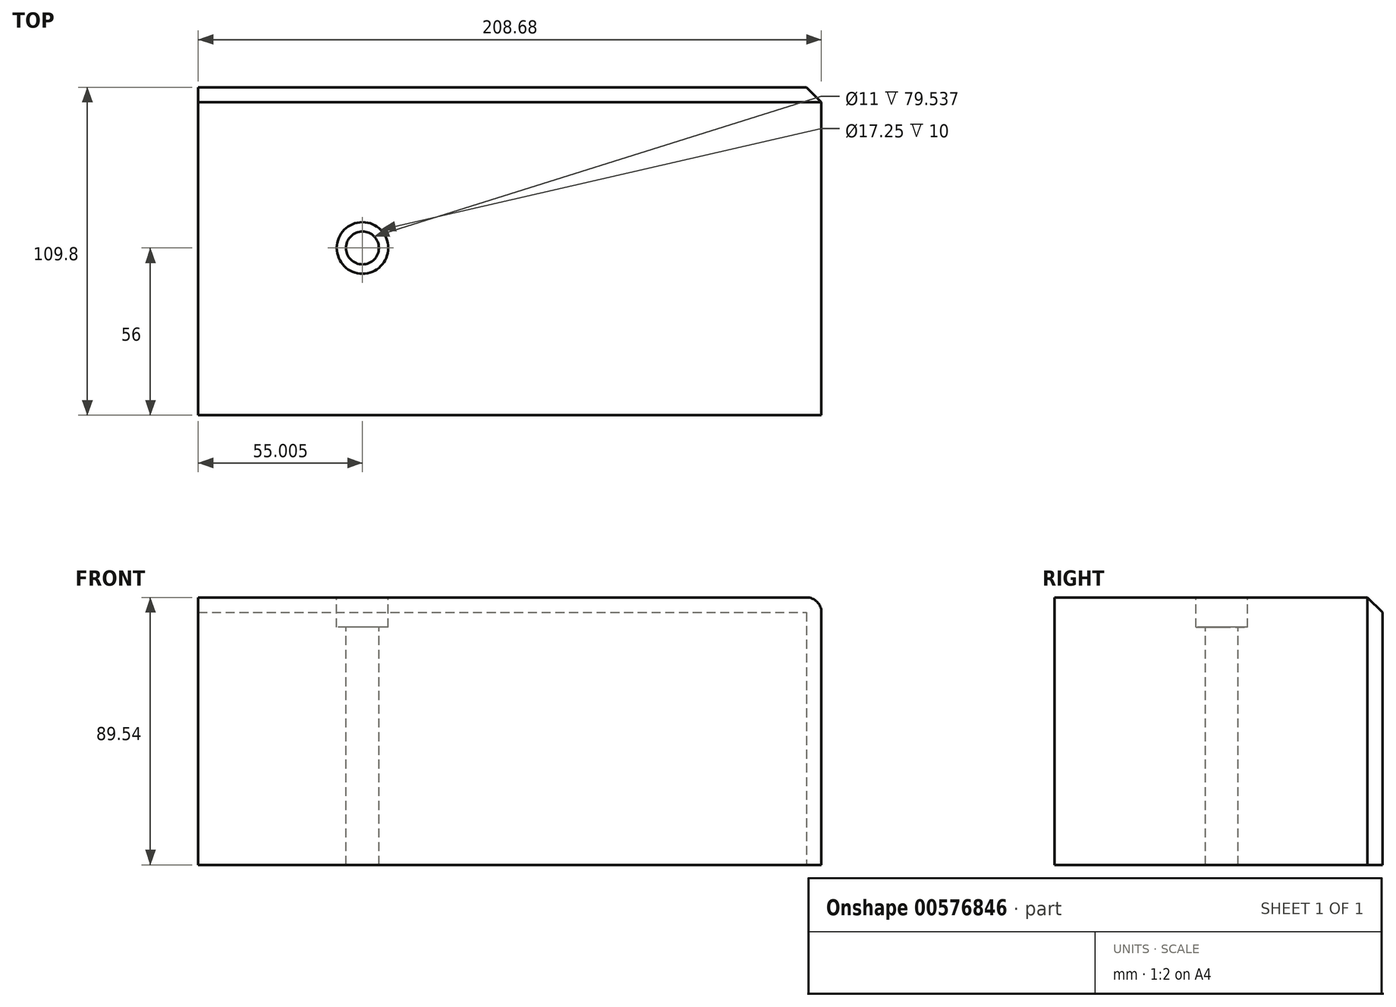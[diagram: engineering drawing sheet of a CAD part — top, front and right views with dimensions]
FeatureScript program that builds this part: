
annotation { "Feature Type Name" : "Feature", "Feature Type Description" : "" }
export const myFeature = defineFeature(function(context is Context, id is Id, definition is map)
    precondition{}
    {
        {
            var Q0;
            Q0=qCreatedBy(makeId("Front.planeOp"),FACE);
            var sketch = newSketch(context, id + "F0", { "sketchPlane" : qUnion([Q0])});
            skLineSegment(sketch, "E0.bottom", {"start": v(-94.92, 55.23) * mm, "end": v(113.76, 55.23) * mm});
            skLineSegment(sketch, "E0.top", {"start": v(-94.92, -34.3) * mm, "end": v(113.76, -34.3) * mm});
            skLineSegment(sketch, "E0.left", {"start": v(-94.92, 55.23) * mm, "end": v(-94.92, -34.3) * mm});
            skLineSegment(sketch, "E0.right", {"start": v(113.76, 55.23) * mm, "end": v(113.76, -34.3) * mm});
            skSolve(sketch);
        }
        {
            var Q0;
            Q0=makeQuery(id+"F0.imprint","IMPRINT",FACE,{"disambiguationData":[TD([[makeQuery(id+"F0.imprint","IMPRINT",EDGE,{"derivedFrom":sQuery(id+"F0.wireOp",EDGE,"E0.bottom")}),-1.0]])]});
            extrude(context, id + "F1", {"entities" : qUnion([Q0]), "depth" : 109.8 * mm, "offsetDistance" : 25 * mm});
        }
        {
            var Q0;
            Q0=makeQuery(id+"F1.opExtrude","SWEPT_FACE",FACE,{"disambiguationData":[OSD([sQuery(id+"F0.wireOp",EDGE,"E0.bottom")])]});
            var sketch = newSketch(context, id + "F2", { "sketchPlane" : qUnion([Q0])});
            skPoint(sketch, "E1", {"position": v(-39.92, -53.8) * mm});
            skSolve(sketch);
        }
        {
            var Q0;
            Q0=sQuery(id+"F2.wireOp",VERTEX,"E1");
            var Q1;
            Q1=makeQuery(id+"F1.opExtrude","SWEPT_BODY",BODY,{"disambiguationData":[OSD([sQuery(id+"F0.wireOp",EDGE,"E0.bottom"),sQuery(id+"F0.wireOp",EDGE,"E0.top"),sQuery(id+"F0.wireOp",EDGE,"E0.left"),sQuery(id+"F0.wireOp",EDGE,"E0.right")])]});
            hole(context, id + "F3", {"style" : HoleStyle.C_BORE, "endStyle" : HoleEndStyle.THROUGH, "standardTappedOrClearance" : lookupTablePath({ "standard" : "ISO", "fit" : "Normal", "size" : "M10", "type" : "Clearance" }), "standardBlindInLast" : lookupTablePath({ "fit" : "Standard", "standard" : "ISO", "size" : "M10", "type" : "Clearance" }), "holeDiameter" : 11 * mm, "cBoreDiameter" : 17.25 * mm, "cBoreDepth" : 10 * mm, "isTappedThrough" : true, "tappedDepth" : 12 * mm, "tapClearance" : 3, "locations" : qUnion([Q0]), "scope" : qUnion([Q1])});
        }
        {
            var Q0;
            Q0=makeQuery(id+"F1.opExtrude","SWEPT_EDGE",EDGE,{"disambiguationData":[OSD([sQuery(id+"F0.wireOp",EDGE,"E0.bottom"),sQuery(id+"F0.wireOp",EDGE,"E0.right")])]});
            fillet(context, id + "F4", {"entities" : qUnion([Q0]), "radius" : 5 * mm, "tangentPropagation" : true, "allowEdgeOverflow" : false});
        }
        {
            var Q0;
            Q0=makeQuery(id+"F1.opExtrude","CAP_EDGE",EDGE,{"disambiguationData":[OSD([sQuery(id+"F0.wireOp",EDGE,"E0.bottom")])],"isStart":true});
            chamfer(context, id + "F5", {"entities" : qUnion([Q0]), "width" : 5 * mm, "tangentPropagation" : true});
        }
    });
